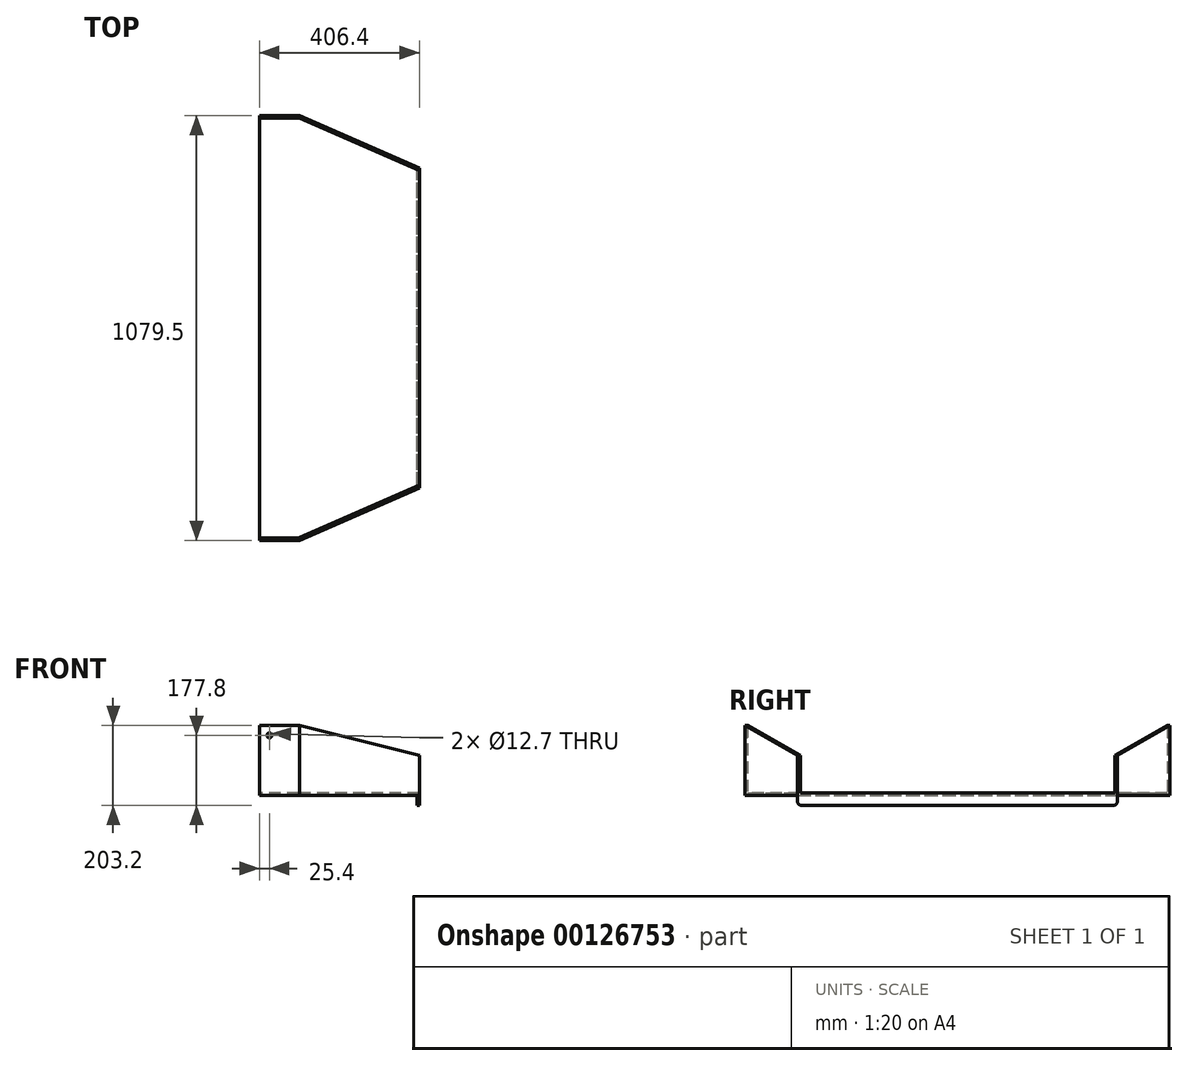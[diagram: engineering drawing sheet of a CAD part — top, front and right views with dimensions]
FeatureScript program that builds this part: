
annotation { "Feature Type Name" : "Feature", "Feature Type Description" : "" }
export const myFeature = defineFeature(function(context is Context, id is Id, definition is map)
    precondition{}
    {
        {
            var Q0;
            Q0=qCreatedBy(makeId("Top.planeOp"),FACE);
            var sketch = newSketch(context, id + "F0", { "sketchPlane" : qUnion([Q0])});
            skLineSegment(sketch, "E0", {"start": v(0, 0) * mm, "end": v(0, 1079.5) * mm});
            skLineSegment(sketch, "E1", {"start": v(0, 1079.5) * mm, "end": v(101.6, 1079.5) * mm});
            skLineSegment(sketch, "E2", {"start": v(101.6, 1079.5) * mm, "end": v(406.4, 946.15) * mm});
            skLineSegment(sketch, "E3", {"start": v(406.4, 133.35) * mm, "end": v(101.6, 0) * mm});
            skLineSegment(sketch, "E4", {"start": v(101.6, 0) * mm, "end": v(0, 0) * mm});
            skLineSegment(sketch, "E5", {"start": v(406.4, 133.35) * mm, "end": v(406.4, 539.75) * mm});
            skLineSegment(sketch, "E6", {"start": v(406.4, 539.75) * mm, "end": v(0, 539.75) * mm, "construction": true});
            skLineSegment(sketch, "E7", {"start": v(406.4, 539.75) * mm, "end": v(406.4, 946.15) * mm});
            skSolve(sketch);
        }
        {
            var Q0;
            Q0 = qSketchRegion(id + "F0", true);
            extrude(context, id + "F1", {"entities" : qUnion([Q0]), "depth" : 177.8 * mm});
        }
        {
            var Q0;
            Q0=makeQuery(id+"F1.opExtrude","CAP_FACE",FACE,{"disambiguationData":[OSD([sQuery(id+"F0.wireOp",EDGE,"E0"),sQuery(id+"F0.wireOp",EDGE,"E1"),sQuery(id+"F0.wireOp",EDGE,"E2"),sQuery(id+"F0.wireOp",EDGE,"E3"),sQuery(id+"F0.wireOp",EDGE,"E4"),sQuery(id+"F0.wireOp",EDGE,"E5"),sQuery(id+"F0.wireOp",EDGE,"E7")])],"isStart":false});
            var Q1;
            Q1=makeQuery(id+"F1.opExtrude","SWEPT_FACE",FACE,{"disambiguationData":[OSD([sQuery(id+"F0.wireOp",EDGE,"E0")])]});
            var Q2;
            Q2=makeQuery(id+"F1.opExtrude","SWEPT_FACE",FACE,{"disambiguationData":[OSD([sQuery(id+"F0.wireOp",EDGE,"E5"),sQuery(id+"F0.wireOp",EDGE,"E7")])]});
            shell(context, id + "F2", {"entities" : qUnion([Q0, Q1, Q2]), "thickness" : 6.35 * mm});
        }
        {
            var Q0;
            Q0=makeQuery(id+"F1.opExtrude","SWEPT_FACE",FACE,{"disambiguationData":[OSD([sQuery(id+"F0.wireOp",EDGE,"E4")])]});
            var sketch = newSketch(context, id + "F3", { "sketchPlane" : qUnion([Q0])});
            skCircle(sketch, "E8", {"center": v(25.4, 152.4) * mm, "radius": 6.35 * mm});
            skLineSegment(sketch, "E9", {"start": v(25.4, 152.4) * mm, "end": v(25.4, 177.8) * mm, "construction": true});
            skLineSegment(sketch, "E10", {"start": v(25.4, 152.4) * mm, "end": v(0, 152.4) * mm, "construction": true});
            skSolve(sketch);
        }
        {
            var Q0;
            Q0 = qSketchRegion(id + "F3", true);
            extrude(context, id + "F4", {"entities" : qUnion([Q0]), "operationType" : NewBodyOperationType.REMOVE, "endBound" : BoundingType.THROUGH_ALL, "oppositeDirection" : true, "depth" : 25.4 * mm});
        }
        {
            var Q0;
            Q0=makeQuery(id+"F1.opExtrude","CAP_FACE",FACE,{"disambiguationData":[OSD([sQuery(id+"F0.wireOp",EDGE,"E0"),sQuery(id+"F0.wireOp",EDGE,"E1"),sQuery(id+"F0.wireOp",EDGE,"E2"),sQuery(id+"F0.wireOp",EDGE,"E3"),sQuery(id+"F0.wireOp",EDGE,"E4"),sQuery(id+"F0.wireOp",EDGE,"E5"),sQuery(id+"F0.wireOp",EDGE,"E7")])],"isStart":true});
            var sketch = newSketch(context, id + "F5", { "sketchPlane" : qUnion([Q0])});
            skLineSegment(sketch, "E11.bottom", {"start": v(406.4, -133.35) * mm, "end": v(400.05, -133.35) * mm});
            skLineSegment(sketch, "E11.top", {"start": v(406.4, -946.15) * mm, "end": v(400.05, -946.15) * mm});
            skLineSegment(sketch, "E11.left", {"start": v(406.4, -133.35) * mm, "end": v(406.4, -946.15) * mm});
            skLineSegment(sketch, "E11.right", {"start": v(400.05, -133.35) * mm, "end": v(400.05, -946.15) * mm});
            skLineSegment(sketch, "E12.bottom", {"start": v(406.4, -946.15) * mm, "end": v(406.4, -946.15) * mm});
            skSolve(sketch);
        }
        {
            var Q0;
            Q0 = qSketchRegion(id + "F5", true);
            extrude(context, id + "F6", {"entities" : qUnion([Q0]), "operationType" : NewBodyOperationType.ADD, "depth" : 25.4 * mm});
        }
        {
            var Q0;
            Q0=qCreatedBy(makeId("Front.planeOp"),FACE);
            var sketch = newSketch(context, id + "F7", { "sketchPlane" : qUnion([Q0])});
            skLineSegment(sketch, "E13.0", {"start": v(406.4, 177.8) * mm, "end": v(101.6, 177.8) * mm});
            skLineSegment(sketch, "E14.0", {"start": v(406.4, 177.8) * mm, "end": v(406.4, 101.6) * mm});
            skLineSegment(sketch, "E15", {"start": v(101.6, 177.8) * mm, "end": v(406.4, 101.6) * mm});
            skPoint(sketch, "E16.orphan", {"position": v(406.4, 0) * mm});
            skSolve(sketch);
        }
        {
            var Q0;
            Q0=makeQuery(id+"F6.opExtrude","CAP_EDGE",EDGE,{"disambiguationData":[OSD([sQuery(id+"F5.wireOp",EDGE,"E11.bottom")])],"isStart":false});
            var Q1;
            Q1=makeQuery(id+"F6.opExtrude","CAP_EDGE",EDGE,{"disambiguationData":[OSD([sQuery(id+"F5.wireOp",EDGE,"E11.top")])],"isStart":false});
            fillet(context, id + "F8", {"entities" : qUnion([Q0, Q1]), "radius" : 10.16 * mm, "tangentPropagation" : true, "allowEdgeOverflow" : false});
        }
        {
            var Q0;
            Q0 = qSketchRegion(id + "F7", true);
            extrude(context, id + "F9", {"entities" : qUnion([Q0]), "operationType" : NewBodyOperationType.REMOVE, "endBound" : BoundingType.THROUGH_ALL, "oppositeDirection" : true, "depth" : 25.4 * mm});
        }
    });
